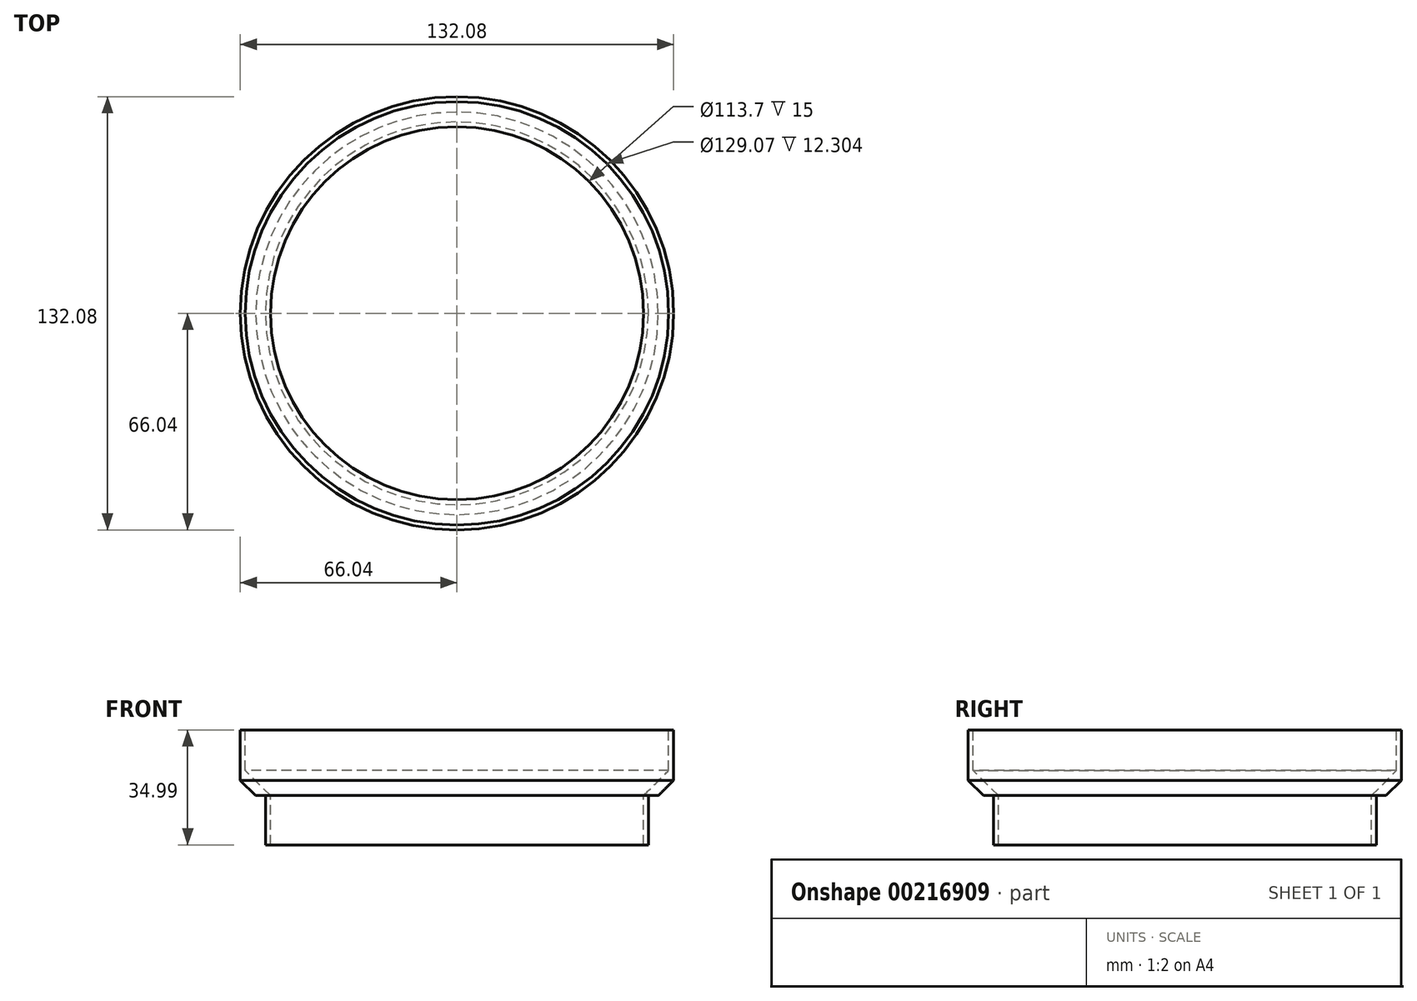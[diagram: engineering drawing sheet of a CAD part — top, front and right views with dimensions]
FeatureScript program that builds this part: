
annotation { "Feature Type Name" : "Feature", "Feature Type Description" : "" }
export const myFeature = defineFeature(function(context is Context, id is Id, definition is map)
    precondition{}
    {
        {
            var Q0;
            Q0=qCreatedBy(makeId("Front.planeOp"),FACE);
            var sketch = newSketch(context, id + "F0", { "sketchPlane" : qUnion([Q0])});
            skLineSegment(sketch, "E0", {"start": v(0, 55.93) * mm, "end": v(0, -56.28) * mm, "construction": true});
            skLineSegment(sketch, "E1.bottom", {"start": v(56.85, 0.01) * mm, "end": v(58.35, 0.01) * mm});
            skLineSegment(sketch, "E1.top", {"start": v(56.85, -14.99) * mm, "end": v(58.35, -14.99) * mm});
            skLineSegment(sketch, "E1.left", {"start": v(56.85, 0.01) * mm, "end": v(56.85, -14.99) * mm});
            skLineSegment(sketch, "E1.right", {"start": v(58.35, 0.01) * mm, "end": v(58.35, -14.99) * mm});
            skLineSegment(sketch, "E2", {"start": v(61.35, 0.01) * mm, "end": v(66.03, 4.7) * mm});
            skLineSegment(sketch, "E3", {"start": v(56.85, 0.01) * mm, "end": v(64.53, 7.7) * mm});
            skLineSegment(sketch, "E4", {"start": v(58.35, 0.01) * mm, "end": v(61.35, 0.01) * mm});
            skLineSegment(sketch, "E5", {"start": v(64.53, 32.05) * mm, "end": v(64.53, 1.62) * mm, "construction": true});
            skLineSegment(sketch, "E6", {"start": v(66.03, 20) * mm, "end": v(66.03, 0) * mm, "construction": true});
            skLineSegment(sketch, "E7", {"start": v(66.03, 4.7) * mm, "end": v(66.03, 20) * mm});
            skLineSegment(sketch, "E8", {"start": v(66.03, 20) * mm, "end": v(64.53, 20) * mm});
            skLineSegment(sketch, "E9", {"start": v(64.53, 7.7) * mm, "end": v(64.53, 20) * mm});
            skSolve(sketch);
        }
        {
            var Q0;
            Q0=makeQuery(id+"F0.imprint","IMPRINT",FACE,{"disambiguationData":[TD([[makeQuery(id+"F0.imprint","IMPRINT",EDGE,{"derivedFrom":sQuery(id+"F0.wireOp",EDGE,"E1.bottom")}),1.0]])]});
            var Q1;
            Q1=makeQuery(id+"F0.imprint","IMPRINT",FACE,{"disambiguationData":[TD([[makeQuery(id+"F0.imprint","IMPRINT",EDGE,{"derivedFrom":sQuery(id+"F0.wireOp",EDGE,"E1.bottom")}),-1.0]])]});
            var Q2;
            Q2=sQuery(id+"F0.wireOp",EDGE,"E0");
            revolve(context, id + "F1", {"entities" : qUnion([Q0, Q1]), "axis" : qUnion([Q2]), "revolveType" : RevolveType.FULL});
        }
    });
